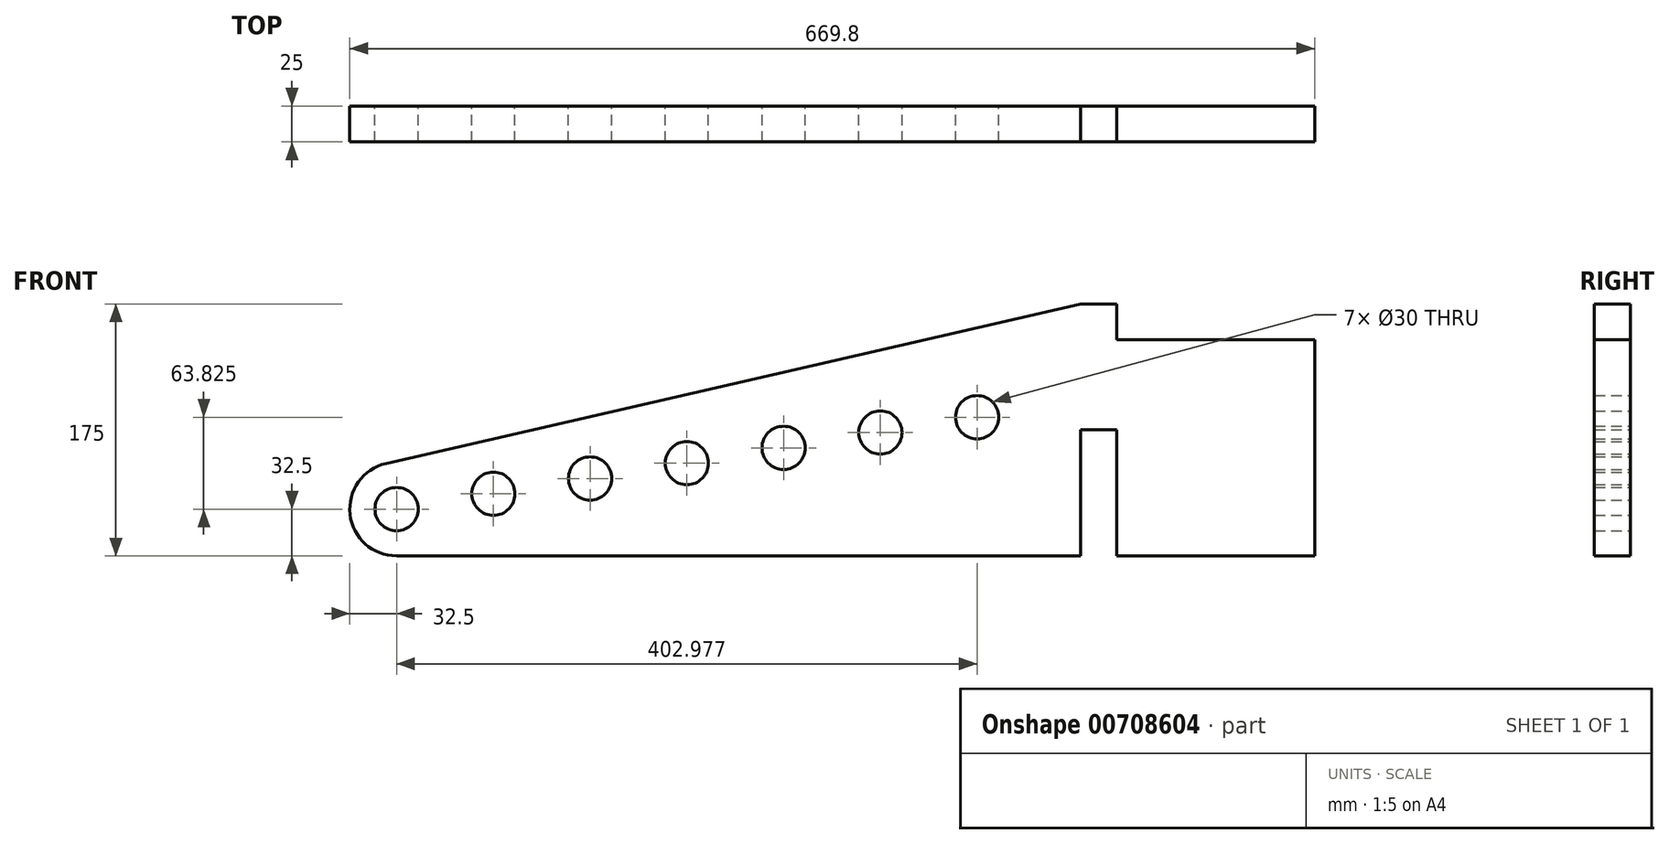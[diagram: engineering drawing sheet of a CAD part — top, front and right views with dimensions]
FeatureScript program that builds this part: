
annotation { "Feature Type Name" : "Feature", "Feature Type Description" : "" }
export const myFeature = defineFeature(function(context is Context, id is Id, definition is map)
    precondition{}
    {
        {
            var Q0;
            Q0=qCreatedBy(makeId("Front.planeOp"),FACE);
            var sketch = newSketch(context, id + "F0", { "sketchPlane" : qUnion([Q0])});
            skLineSegment(sketch, "E0", {"start": v(-7.28, 31.67) * mm, "end": v(474.8, 142.5) * mm});
            skLineSegment(sketch, "E1", {"start": v(474.8, 142.5) * mm, "end": v(499.8, 142.5) * mm});
            skLineSegment(sketch, "E2", {"start": v(499.8, 142.5) * mm, "end": v(499.8, 117.5) * mm});
            skLineSegment(sketch, "E3", {"start": v(499.8, 117.5) * mm, "end": v(637.3, 117.5) * mm});
            skLineSegment(sketch, "E4", {"start": v(637.3, 117.5) * mm, "end": v(637.3, -32.5) * mm});
            skLineSegment(sketch, "E5", {"start": v(637.3, -32.5) * mm, "end": v(499.8, -32.5) * mm});
            skPoint(sketch, "E5.endSnap0", {"position": v(0, 0) * mm});
            skLineSegment(sketch, "E6", {"start": v(499.8, -32.5) * mm, "end": v(499.8, 55) * mm});
            skLineSegment(sketch, "E7", {"start": v(499.8, 55) * mm, "end": v(474.8, 55) * mm});
            skLineSegment(sketch, "E8", {"start": v(474.8, 55) * mm, "end": v(474.8, -32.5) * mm});
            skLineSegment(sketch, "E9", {"start": v(474.8, -32.5) * mm, "end": v(0, -32.5) * mm});
            skCircle(sketch, "E10", {"center": v(0, 0) * mm, "radius": 15 * mm});
            skLineSegment(sketch, "E11", {"start": v(0, 0) * mm, "end": v(14.74, 2.77) * mm});
            skCircle(sketch, "E12.1.0.0", {"center": v(67.16, 10.64) * mm, "radius": 15 * mm});
            skCircle(sketch, "E12.2.0.0", {"center": v(134.33, 21.28) * mm, "radius": 15 * mm});
            skCircle(sketch, "E12.3.0.0", {"center": v(201.49, 31.91) * mm, "radius": 15 * mm});
            skCircle(sketch, "E12.4.0.0", {"center": v(268.65, 42.55) * mm, "radius": 15 * mm});
            skCircle(sketch, "E12.5.0.0", {"center": v(335.81, 53.19) * mm, "radius": 15 * mm});
            skCircle(sketch, "E12.6.0.0", {"center": v(402.98, 63.83) * mm, "radius": 15 * mm});
            skLineSegment(sketch, "E12.direction1", {"start": v(0, 0) * mm, "end": v(67.16, 10.64) * mm, "construction": true});
            skArc(sketch, "E13", {"start": v(-7.28, 31.67) * mm, "mid": v(-32.3, -3.66) * mm, "end": v(0, -32.5) * mm});
            skSolve(sketch);
        }
        {
            var Q0;
            Q0=makeQuery(id+"F0.imprint","IMPRINT",FACE,{"disambiguationData":[TD([[makeQuery(id+"F0.imprint","IMPRINT",EDGE,{"derivedFrom":sQuery(id+"F0.wireOp",EDGE,"E0")}),-1.0]])]});
            extrude(context, id + "F1", {"entities" : qUnion([Q0]), "depth" : 25 * mm, "offsetDistance" : 25 * mm});
        }
    });
